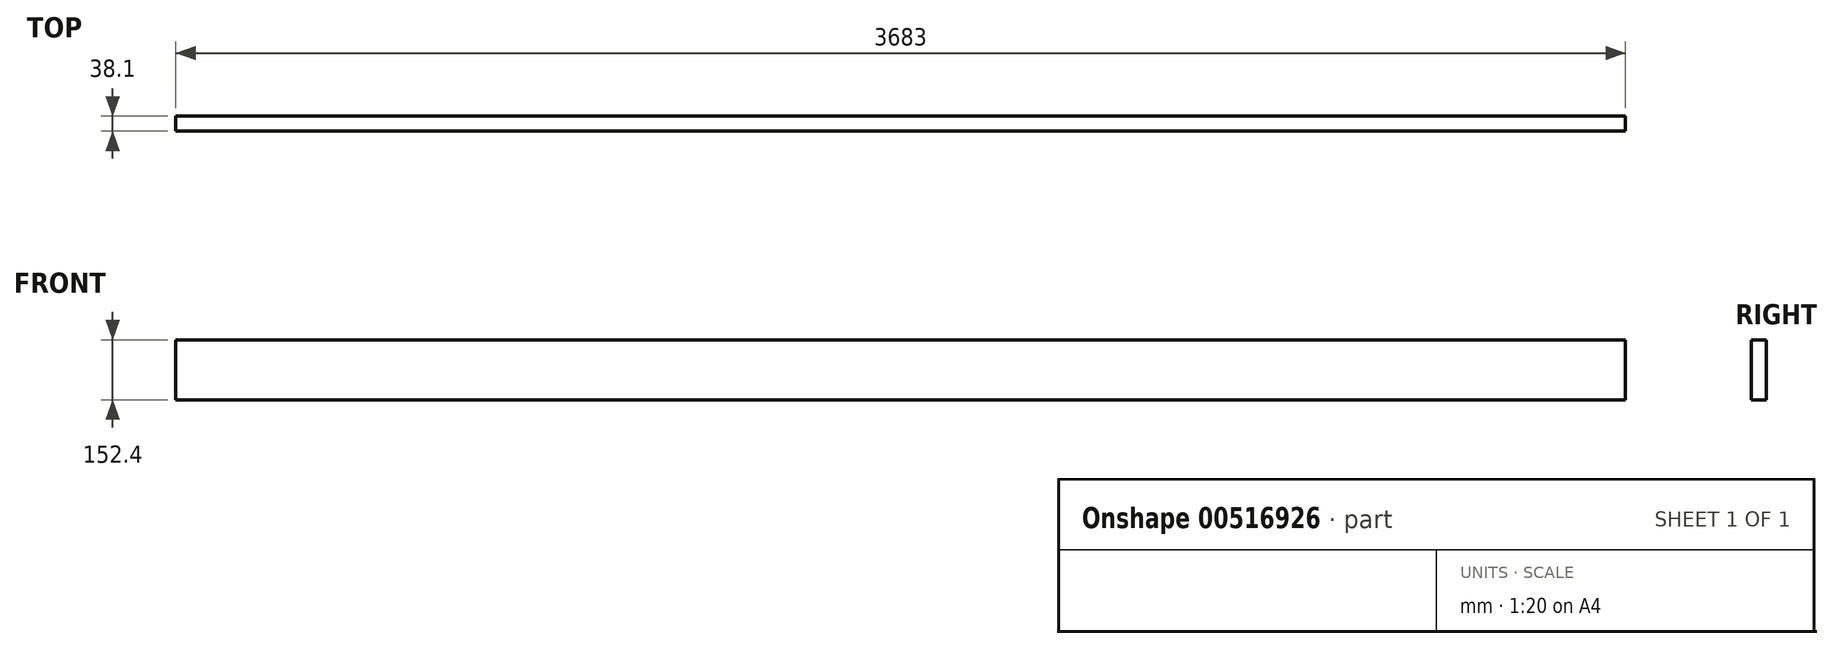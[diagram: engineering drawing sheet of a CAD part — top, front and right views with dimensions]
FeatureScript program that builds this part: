
annotation { "Feature Type Name" : "Feature", "Feature Type Description" : "" }
export const myFeature = defineFeature(function(context is Context, id is Id, definition is map)
    precondition{}
    {
        {
            var Q0;
            Q0=qCreatedBy(makeId("Front.planeOp"),FACE);
            var sketch = newSketch(context, id + "F0", { "sketchPlane" : qUnion([Q0])});
            skLineSegment(sketch, "E0.bottom", {"start": v(0, 0) * mm, "end": v(3683, 0) * mm});
            skLineSegment(sketch, "E0.top", {"start": v(0, 152.4) * mm, "end": v(3683, 152.4) * mm});
            skLineSegment(sketch, "E0.left", {"start": v(0, 0) * mm, "end": v(0, 152.4) * mm});
            skLineSegment(sketch, "E0.right", {"start": v(3683, 0) * mm, "end": v(3683, 152.4) * mm});
            skSolve(sketch);
        }
        {
            var Q0;
            Q0 = qSketchRegion(id + "F0", true);
            extrude(context, id + "F1", {"entities" : qUnion([Q0]), "depth" : 38.1 * mm, "offsetDistance" : 25.4 * mm});
        }
    });
